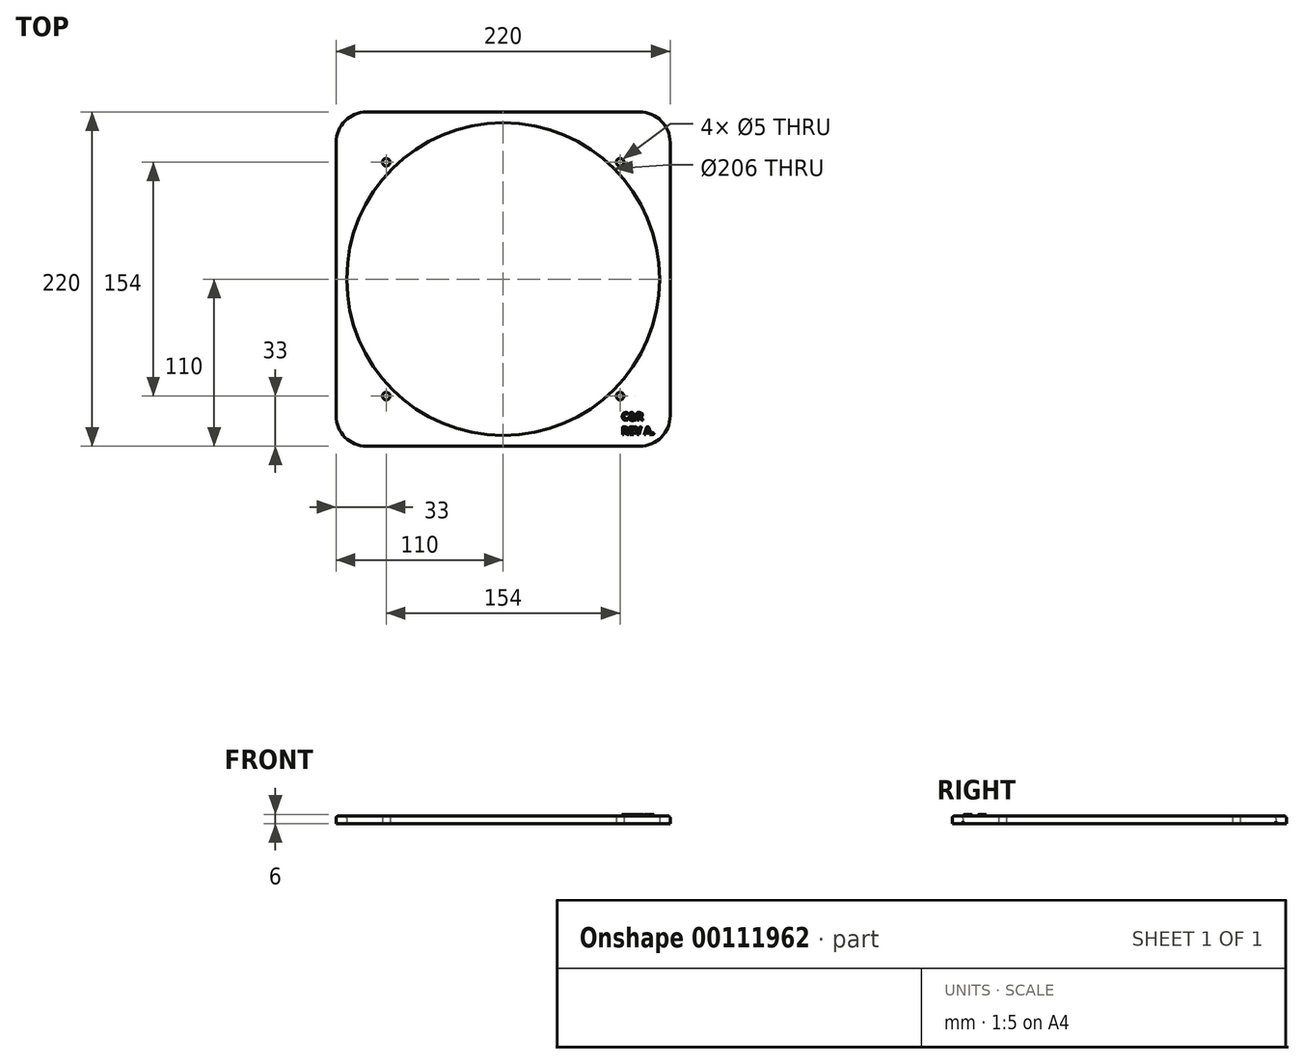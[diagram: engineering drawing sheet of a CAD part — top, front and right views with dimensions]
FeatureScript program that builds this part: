
annotation { "Feature Type Name" : "Feature", "Feature Type Description" : "" }
export const myFeature = defineFeature(function(context is Context, id is Id, definition is map)
    precondition{}
    {
        {
            var Q0;
            Q0=qCreatedBy(makeId("Top.planeOp"),FACE);
            var sketch = newSketch(context, id + "F0", { "sketchPlane" : qUnion([Q0])});
            skLineSegment(sketch, "E0.bottom", {"start": v(90, -110) * mm, "end": v(-90, -110) * mm});
            skLineSegment(sketch, "E0.top", {"start": v(90, 110) * mm, "end": v(-90, 110) * mm});
            skLineSegment(sketch, "E0.left", {"start": v(110, -90) * mm, "end": v(110, 90) * mm});
            skLineSegment(sketch, "E0.right", {"start": v(-110, -90) * mm, "end": v(-110, 90) * mm});
            skPoint(sketch, "E0.middle", {"position": v(0, 0) * mm});
            skCircle(sketch, "E1", {"center": v(0, 0) * mm, "radius": 103 * mm});
            skPoint(sketch, "E2.visualSharp", {"position": v(110, -110) * mm});
            skArc(sketch, "E2.filletArc", {"start": v(90, -110) * mm, "mid": v(104.14, -104.14) * mm, "end": v(110, -90) * mm});
            skPoint(sketch, "E3.visualSharp", {"position": v(-110, -110) * mm});
            skArc(sketch, "E3.filletArc", {"start": v(-110, -90) * mm, "mid": v(-104.14, -104.14) * mm, "end": v(-90, -110) * mm});
            skPoint(sketch, "E4.visualSharp", {"position": v(-110, 110) * mm});
            skArc(sketch, "E4.filletArc", {"start": v(-90, 110) * mm, "mid": v(-104.14, 104.14) * mm, "end": v(-110, 90) * mm});
            skPoint(sketch, "E5.visualSharp", {"position": v(110, 110) * mm});
            skArc(sketch, "E5.filletArc", {"start": v(110, 90) * mm, "mid": v(104.14, 104.14) * mm, "end": v(90, 110) * mm});
            skSolve(sketch);
        }
        {
            var Q0;
            Q0=qSketchRegion(id+"F0",true);
            extrude(context, id + "F1", {"entities" : qUnion([Q0]), "depth" : 5 * mm});
        }
        {
            var Q0;
            Q0=makeQuery(id+"F1.opExtrude","CAP_FACE",FACE,{"disambiguationData":[OSD([sQuery(id+"F0.wireOp",EDGE,"E0.bottom"),sQuery(id+"F0.wireOp",EDGE,"E0.top"),sQuery(id+"F0.wireOp",EDGE,"E0.left"),sQuery(id+"F0.wireOp",EDGE,"E0.right"),sQuery(id+"F0.wireOp",EDGE,"E1")])],"isStart":true});
            var sketch = newSketch(context, id + "F2", { "sketchPlane" : qUnion([Q0])});
            skLineSegment(sketch, "E6", {"start": v(0, -110) * mm, "end": v(0, 110) * mm, "construction": true});
            skPoint(sketch, "E6.endSnap0", {"position": v(0, 110) * mm});
            skLineSegment(sketch, "E7", {"start": v(-110, 0) * mm, "end": v(110, 0) * mm, "construction": true});
            skPoint(sketch, "E8", {"position": v(0, 0) * mm});
            skCircle(sketch, "E9", {"center": v(-77, 77) * mm, "radius": 2.5 * mm});
            skCircle(sketch, "E10.1.0", {"center": v(-77, -77) * mm, "radius": 2.5 * mm});
            skCircle(sketch, "E10.2.0", {"center": v(77, -77) * mm, "radius": 2.5 * mm});
            skCircle(sketch, "E10.3.0", {"center": v(77, 77) * mm, "radius": 2.5 * mm});
            skSolve(sketch);
        }
        {
            var Q0;
            Q0 = qSketchRegion(id + "F2", true);
            extrude(context, id + "F3", {"entities" : qUnion([Q0]), "operationType" : NewBodyOperationType.REMOVE, "endBound" : BoundingType.UP_TO_NEXT, "oppositeDirection" : true, "depth" : 5 * mm});
        }
        {
            var Q0;
            Q0=makeQuery(id+"F1.opExtrude","CAP_EDGE",EDGE,{"disambiguationData":[OSD([sQuery(id+"F0.wireOp",EDGE,"E3.filletArc")])],"isStart":false});
            var Q1;
            Q1=makeQuery(id+"F1.opExtrude","CAP_EDGE",EDGE,{"disambiguationData":[OSD([sQuery(id+"F0.wireOp",EDGE,"E1")])],"isStart":false});
            var Q2;
            Q2=makeQuery(id+"F1.opExtrude","CAP_EDGE",EDGE,{"disambiguationData":[OSD([sQuery(id+"F0.wireOp",EDGE,"E1")])],"isStart":true});
            fillet(context, id + "F4", {"entities" : qUnion([Q0, Q1, Q2]), "radius" : 1.5 * mm, "tangentPropagation" : true, "allowEdgeOverflow" : false});
        }
        {
            var Q0;
            Q0=makeQuery(id+"F1.opExtrude","CAP_FACE",FACE,{"disambiguationData":[OSD([sQuery(id+"F0.wireOp",EDGE,"E0.bottom"),sQuery(id+"F0.wireOp",EDGE,"E0.top"),sQuery(id+"F0.wireOp",EDGE,"E0.left"),sQuery(id+"F0.wireOp",EDGE,"E0.right"),sQuery(id+"F0.wireOp",EDGE,"E1"),sQuery(id+"F0.wireOp",EDGE,"E2.filletArc"),sQuery(id+"F0.wireOp",EDGE,"E3.filletArc"),sQuery(id+"F0.wireOp",EDGE,"E4.filletArc"),sQuery(id+"F0.wireOp",EDGE,"E5.filletArc")])],"isStart":false});
            var sketch = newSketch(context, id + "F5", { "sketchPlane" : qUnion([Q0])});
            skText(sketch, "E11", { "text": "C&R\nREV A.", "fontName": "OpenSans-Bold.ttf"});
            const initialGuessF5  = {"E11": [0.07805, -0.09286, 1, 0, 0.005]};
            skSetInitialGuess(sketch, initialGuessF5);
            skSolve(sketch);
        }
        {
            var Q0;
            Q0 = qSketchRegion(id + "F5", true);
            extrude(context, id + "F6", {"entities" : qUnion([Q0]), "operationType" : NewBodyOperationType.ADD, "depth" : 1 * mm});
        }
        {
            var Q0;
            Q0=makeQuery(id+"F6.opExtrude","CAP_EDGE",EDGE,{"disambiguationData":[OSD([sQuery(id+"F5.wireOp",EDGE,"E11.sketch_text.stroke-6")])],"isStart":false});
            var Q1;
            Q1=makeQuery(id+"F6.opExtrude","CAP_EDGE",EDGE,{"disambiguationData":[OSD([sQuery(id+"F5.wireOp",EDGE,"E11.sketch_text.stroke-4")])],"isStart":false});
            var Q2;
            Q2=makeQuery(id+"F6.opExtrude","CAP_EDGE",EDGE,{"disambiguationData":[OSD([sQuery(id+"F5.wireOp",EDGE,"E11.sketch_text.stroke-3")])],"isStart":false});
            var Q3;
            Q3=makeQuery(id+"F6.opExtrude","CAP_EDGE",EDGE,{"disambiguationData":[OSD([sQuery(id+"F5.wireOp",EDGE,"E11.sketch_text.stroke-12")])],"isStart":false});
            var Q4;
            Q4=makeQuery(id+"F6.opExtrude","CAP_EDGE",EDGE,{"disambiguationData":[OSD([sQuery(id+"F5.wireOp",EDGE,"E11.sketch_text.stroke-19")])],"isStart":false});
            var Q5;
            Q5=makeQuery(id+"F6.opExtrude","CAP_EDGE",EDGE,{"disambiguationData":[OSD([sQuery(id+"F5.wireOp",EDGE,"E11.sketch_text.stroke-22")])],"isStart":false});
            var Q6;
            Q6=makeQuery(id+"F6.opExtrude","CAP_EDGE",EDGE,{"disambiguationData":[OSD([sQuery(id+"F5.wireOp",EDGE,"E11.sketch_text.stroke-43")])],"isStart":false});
            var Q7;
            Q7=makeQuery(id+"F6.opExtrude","CAP_EDGE",EDGE,{"disambiguationData":[OSD([sQuery(id+"F5.wireOp",EDGE,"E11.sketch_text.stroke-39")])],"isStart":false});
            var Q8;
            Q8=makeQuery(id+"F6.opExtrude","CAP_EDGE",EDGE,{"disambiguationData":[OSD([sQuery(id+"F5.wireOp",EDGE,"E11.sketch_text.stroke-38")])],"isStart":false});
            var Q9;
            Q9=makeQuery(id+"F6.opExtrude","CAP_EDGE",EDGE,{"disambiguationData":[OSD([sQuery(id+"F5.wireOp",EDGE,"E11.sketch_text.stroke-31")])],"isStart":false});
            var Q10;
            Q10=makeQuery(id+"F6.opExtrude","CAP_EDGE",EDGE,{"disambiguationData":[OSD([sQuery(id+"F5.wireOp",EDGE,"E11.sketch_text.stroke-32")])],"isStart":false});
            var Q11;
            Q11=makeQuery(id+"F6.opExtrude","CAP_EDGE",EDGE,{"disambiguationData":[OSD([sQuery(id+"F5.wireOp",EDGE,"E11.sketch_text.stroke-35")])],"isStart":false});
            var Q12;
            Q12=makeQuery(id+"F6.opExtrude","CAP_EDGE",EDGE,{"disambiguationData":[OSD([sQuery(id+"F5.wireOp",EDGE,"E11.sketch_text.stroke-33")])],"isStart":false});
            var Q13;
            Q13=makeQuery(id+"F6.opExtrude","CAP_EDGE",EDGE,{"disambiguationData":[OSD([sQuery(id+"F5.wireOp",EDGE,"E11.sketch_text.stroke-15")])],"isStart":false});
            var Q14;
            Q14=makeQuery(id+"F6.opExtrude","CAP_EDGE",EDGE,{"disambiguationData":[OSD([sQuery(id+"F5.wireOp",EDGE,"E11.sketch_text.stroke-16")])],"isStart":false});
            var Q15;
            Q15=makeQuery(id+"F6.opExtrude","CAP_EDGE",EDGE,{"disambiguationData":[OSD([sQuery(id+"F5.wireOp",EDGE,"E11.sketch_text.stroke-57")])],"isStart":false});
            var Q16;
            Q16=makeQuery(id+"F6.opExtrude","CAP_EDGE",EDGE,{"disambiguationData":[OSD([sQuery(id+"F5.wireOp",EDGE,"E11.sketch_text.stroke-58")])],"isStart":false});
            var Q17;
            Q17=makeQuery(id+"F6.opExtrude","CAP_EDGE",EDGE,{"disambiguationData":[OSD([sQuery(id+"F5.wireOp",EDGE,"E11.sketch_text.stroke-56")])],"isStart":false});
            var Q18;
            Q18=makeQuery(id+"F6.opExtrude","CAP_EDGE",EDGE,{"disambiguationData":[OSD([sQuery(id+"F5.wireOp",EDGE,"E11.sketch_text.stroke-66")])],"isStart":false});
            var Q19;
            Q19=makeQuery(id+"F6.opExtrude","CAP_EDGE",EDGE,{"disambiguationData":[OSD([sQuery(id+"F5.wireOp",EDGE,"E11.sketch_text.stroke-67")])],"isStart":false});
            var Q20;
            Q20=makeQuery(id+"F6.opExtrude","CAP_EDGE",EDGE,{"disambiguationData":[OSD([sQuery(id+"F5.wireOp",EDGE,"E11.sketch_text.stroke-64")])],"isStart":false});
            var Q21;
            Q21=makeQuery(id+"F6.opExtrude","CAP_EDGE",EDGE,{"disambiguationData":[OSD([sQuery(id+"F5.wireOp",EDGE,"E11.sketch_text.stroke-63")])],"isStart":false});
            var Q22;
            Q22=makeQuery(id+"F6.opExtrude","CAP_EDGE",EDGE,{"disambiguationData":[OSD([sQuery(id+"F5.wireOp",EDGE,"E11.sketch_text.stroke-50")])],"isStart":false});
            var Q23;
            Q23=makeQuery(id+"F6.opExtrude","CAP_EDGE",EDGE,{"disambiguationData":[OSD([sQuery(id+"F5.wireOp",EDGE,"E11.sketch_text.stroke-65")])],"isStart":false});
            var Q24;
            Q24=makeQuery(id+"F6.opExtrude","CAP_EDGE",EDGE,{"disambiguationData":[OSD([sQuery(id+"F5.wireOp",EDGE,"E11.sketch_text.stroke-55")])],"isStart":false});
            var Q25;
            Q25=makeQuery(id+"F6.opExtrude","CAP_EDGE",EDGE,{"disambiguationData":[OSD([sQuery(id+"F5.wireOp",EDGE,"E11.sketch_text.stroke-69")])],"isStart":false});
            var Q26;
            Q26=makeQuery(id+"F6.opExtrude","CAP_EDGE",EDGE,{"disambiguationData":[OSD([sQuery(id+"F5.wireOp",EDGE,"E11.sketch_text.stroke-74")])],"isStart":false});
            var Q27;
            Q27=makeQuery(id+"F6.opExtrude","CAP_EDGE",EDGE,{"disambiguationData":[OSD([sQuery(id+"F5.wireOp",EDGE,"E11.sketch_text.stroke-78")])],"isStart":false});
            var Q28;
            Q28=makeQuery(id+"F6.opExtrude","CAP_EDGE",EDGE,{"disambiguationData":[OSD([sQuery(id+"F5.wireOp",EDGE,"E11.sketch_text.stroke-77")])],"isStart":false});
            var Q29;
            Q29=makeQuery(id+"F6.opExtrude","CAP_EDGE",EDGE,{"disambiguationData":[OSD([sQuery(id+"F5.wireOp",EDGE,"E11.sketch_text.stroke-76")])],"isStart":false});
            var Q30;
            Q30=makeQuery(id+"F6.opExtrude","CAP_EDGE",EDGE,{"disambiguationData":[OSD([sQuery(id+"F5.wireOp",EDGE,"E11.sketch_text.stroke-75")])],"isStart":false});
            var Q31;
            Q31=makeQuery(id+"F6.opExtrude","CAP_EDGE",EDGE,{"disambiguationData":[OSD([sQuery(id+"F5.wireOp",EDGE,"E11.sketch_text.stroke-86")])],"isStart":false});
            var Q32;
            Q32=makeQuery(id+"F6.opExtrude","CAP_EDGE",EDGE,{"disambiguationData":[OSD([sQuery(id+"F5.wireOp",EDGE,"E11.sketch_text.stroke-85")])],"isStart":false});
            var Q33;
            Q33=makeQuery(id+"F6.opExtrude","CAP_EDGE",EDGE,{"disambiguationData":[OSD([sQuery(id+"F5.wireOp",EDGE,"E11.sketch_text.stroke-83")])],"isStart":false});
            var Q34;
            Q34=makeQuery(id+"F6.opExtrude","CAP_EDGE",EDGE,{"disambiguationData":[OSD([sQuery(id+"F5.wireOp",EDGE,"E11.sketch_text.stroke-84")])],"isStart":false});
            var Q35;
            Q35=makeQuery(id+"F6.opExtrude","CAP_EDGE",EDGE,{"disambiguationData":[OSD([sQuery(id+"F5.wireOp",EDGE,"E11.sketch_text.stroke-87")])],"isStart":false});
            var Q36;
            Q36=makeQuery(id+"F6.opExtrude","CAP_EDGE",EDGE,{"disambiguationData":[OSD([sQuery(id+"F5.wireOp",EDGE,"E11.sketch_text.stroke-98")])],"isStart":false});
            var Q37;
            Q37=makeQuery(id+"F6.opExtrude","CAP_EDGE",EDGE,{"disambiguationData":[OSD([sQuery(id+"F5.wireOp",EDGE,"E11.sketch_text.stroke-97")])],"isStart":false});
            var Q38;
            Q38=makeQuery(id+"F6.opExtrude","CAP_EDGE",EDGE,{"disambiguationData":[OSD([sQuery(id+"F5.wireOp",EDGE,"E11.sketch_text.stroke-96")])],"isStart":false});
            var Q39;
            Q39=makeQuery(id+"F6.opExtrude","CAP_EDGE",EDGE,{"disambiguationData":[OSD([sQuery(id+"F5.wireOp",EDGE,"E11.sketch_text.stroke-95")])],"isStart":false});
            var Q40;
            Q40=makeQuery(id+"F6.opExtrude","CAP_EDGE",EDGE,{"disambiguationData":[OSD([sQuery(id+"F5.wireOp",EDGE,"E11.sketch_text.stroke-94")])],"isStart":false});
            var Q41;
            Q41=makeQuery(id+"F6.opExtrude","CAP_EDGE",EDGE,{"disambiguationData":[OSD([sQuery(id+"F5.wireOp",EDGE,"E11.sketch_text.stroke-93")])],"isStart":false});
            var Q42;
            Q42=makeQuery(id+"F6.opExtrude","CAP_EDGE",EDGE,{"disambiguationData":[OSD([sQuery(id+"F5.wireOp",EDGE,"E11.sketch_text.stroke-92")])],"isStart":false});
            var Q43;
            Q43=makeQuery(id+"F6.opExtrude","CAP_EDGE",EDGE,{"disambiguationData":[OSD([sQuery(id+"F5.wireOp",EDGE,"E11.sketch_text.stroke-91")])],"isStart":false});
            var Q44;
            Q44=makeQuery(id+"F6.opExtrude","CAP_EDGE",EDGE,{"disambiguationData":[OSD([sQuery(id+"F5.wireOp",EDGE,"E11.sketch_text.stroke-90")])],"isStart":false});
            var Q45;
            Q45=makeQuery(id+"F6.opExtrude","CAP_EDGE",EDGE,{"disambiguationData":[OSD([sQuery(id+"F5.wireOp",EDGE,"E11.sketch_text.stroke-89")])],"isStart":false});
            var Q46;
            Q46=makeQuery(id+"F6.opExtrude","CAP_EDGE",EDGE,{"disambiguationData":[OSD([sQuery(id+"F5.wireOp",EDGE,"E11.sketch_text.stroke-88")])],"isStart":false});
            var Q47;
            Q47=makeQuery(id+"F6.opExtrude","CAP_EDGE",EDGE,{"disambiguationData":[OSD([sQuery(id+"F5.wireOp",EDGE,"E11.sketch_text.stroke-102")])],"isStart":false});
            var Q48;
            Q48=makeQuery(id+"F6.opExtrude","CAP_EDGE",EDGE,{"disambiguationData":[OSD([sQuery(id+"F5.wireOp",EDGE,"E11.sketch_text.stroke-104")])],"isStart":false});
            var Q49;
            Q49=makeQuery(id+"F6.opExtrude","CAP_EDGE",EDGE,{"disambiguationData":[OSD([sQuery(id+"F5.wireOp",EDGE,"E11.sketch_text.stroke-100")])],"isStart":false});
            var Q50;
            Q50=makeQuery(id+"F6.opExtrude","CAP_EDGE",EDGE,{"disambiguationData":[OSD([sQuery(id+"F5.wireOp",EDGE,"E11.sketch_text.stroke-101")])],"isStart":false});
            var Q51;
            Q51=makeQuery(id+"F6.opExtrude","CAP_EDGE",EDGE,{"disambiguationData":[OSD([sQuery(id+"F5.wireOp",EDGE,"E11.sketch_text.stroke-103")])],"isStart":false});
            var Q52;
            Q52=makeQuery(id+"F6.opExtrude","CAP_EDGE",EDGE,{"disambiguationData":[OSD([sQuery(id+"F5.wireOp",EDGE,"E11.sketch_text.stroke-99")])],"isStart":false});
            var Q53;
            Q53=makeQuery(id+"F6.opExtrude","CAP_EDGE",EDGE,{"disambiguationData":[OSD([sQuery(id+"F5.wireOp",EDGE,"E11.sketch_text.stroke-112")])],"isStart":false});
            var Q54;
            Q54=makeQuery(id+"F6.opExtrude","CAP_EDGE",EDGE,{"disambiguationData":[OSD([sQuery(id+"F5.wireOp",EDGE,"E11.sketch_text.stroke-111")])],"isStart":false});
            var Q55;
            Q55=makeQuery(id+"F6.opExtrude","CAP_EDGE",EDGE,{"disambiguationData":[OSD([sQuery(id+"F5.wireOp",EDGE,"E11.sketch_text.stroke-110")])],"isStart":false});
            var Q56;
            Q56=makeQuery(id+"F6.opExtrude","CAP_EDGE",EDGE,{"disambiguationData":[OSD([sQuery(id+"F5.wireOp",EDGE,"E11.sketch_text.stroke-109")])],"isStart":false});
            var Q57;
            Q57=makeQuery(id+"F6.opExtrude","CAP_EDGE",EDGE,{"disambiguationData":[OSD([sQuery(id+"F5.wireOp",EDGE,"E11.sketch_text.stroke-116")])],"isStart":false});
            var Q58;
            Q58=makeQuery(id+"F6.opExtrude","CAP_EDGE",EDGE,{"disambiguationData":[OSD([sQuery(id+"F5.wireOp",EDGE,"E11.sketch_text.stroke-127")])],"isStart":false});
            var Q59;
            Q59=makeQuery(id+"F6.opExtrude","CAP_EDGE",EDGE,{"disambiguationData":[OSD([sQuery(id+"F5.wireOp",EDGE,"E11.sketch_text.stroke-115")])],"isStart":false});
            var Q60;
            Q60=makeQuery(id+"F6.opExtrude","CAP_EDGE",EDGE,{"disambiguationData":[OSD([sQuery(id+"F5.wireOp",EDGE,"E11.sketch_text.stroke-117")])],"isStart":false});
            var Q61;
            Q61=makeQuery(id+"F6.opExtrude","CAP_EDGE",EDGE,{"disambiguationData":[OSD([sQuery(id+"F5.wireOp",EDGE,"E11.sketch_text.stroke-120")])],"isStart":false});
            var Q62;
            Q62=makeQuery(id+"F6.opExtrude","CAP_EDGE",EDGE,{"disambiguationData":[OSD([sQuery(id+"F5.wireOp",EDGE,"E11.sketch_text.stroke-118")])],"isStart":false});
            var Q63;
            Q63=makeQuery(id+"F6.opExtrude","CAP_EDGE",EDGE,{"disambiguationData":[OSD([sQuery(id+"F5.wireOp",EDGE,"E11.sketch_text.stroke-113")])],"isStart":false});
            fillet(context, id + "F7", {"entities" : qUnion([Q0, Q1, Q2, Q3, Q4, Q5, Q6, Q7, Q8, Q9, Q10, Q11, Q12, Q13, Q14, Q15, Q16, Q17, Q18, Q19, Q20, Q21, Q22, Q23, Q24, Q25, Q26, Q27, Q28, Q29, Q30, Q31, Q32, Q33, Q34, Q35, Q36, Q37, Q38, Q39, Q40, Q41, Q42, Q43, Q44, Q45, Q46, Q47, Q48, Q49, Q50, Q51, Q52, Q53, Q54, Q55, Q56, Q57, Q58, Q59, Q60, Q61, Q62, Q63]), "radius" : .3 * mm, "tangentPropagation" : true, "allowEdgeOverflow" : false});
        }
        {
            var Q0;
            Q0=makeQuery(id+"F6.opExtrude","CAP_EDGE",EDGE,{"disambiguationData":[OSD([sQuery(id+"F5.wireOp",EDGE,"E11.sketch_text.stroke-114")])],"isStart":false});
            fillet(context, id + "F8", {"entities" : qUnion([Q0]), "radius" : .3 * mm, "tangentPropagation" : true, "allowEdgeOverflow" : false});
        }
        {
            var Q0;
            Q0=makeQuery(id+"F6.opExtrude","CAP_EDGE",EDGE,{"disambiguationData":[OSD([sQuery(id+"F5.wireOp",EDGE,"E11.sketch_text.stroke-119")])],"isStart":false});
            fillet(context, id + "F9", {"entities" : qUnion([Q0]), "radius" : .3 * mm, "tangentPropagation" : true, "allowEdgeOverflow" : false});
        }
        {
            var Q0;
            Q0=makeQuery(id+"F6.opExtrude","CAP_EDGE",EDGE,{"disambiguationData":[OSD([sQuery(id+"F5.wireOp",EDGE,"E11.sketch_text.stroke-108")])],"isStart":false});
            fillet(context, id + "F10", {"entities" : qUnion([Q0]), "radius" : .20 * mm, "tangentPropagation" : true, "allowEdgeOverflow" : false});
        }
    });
